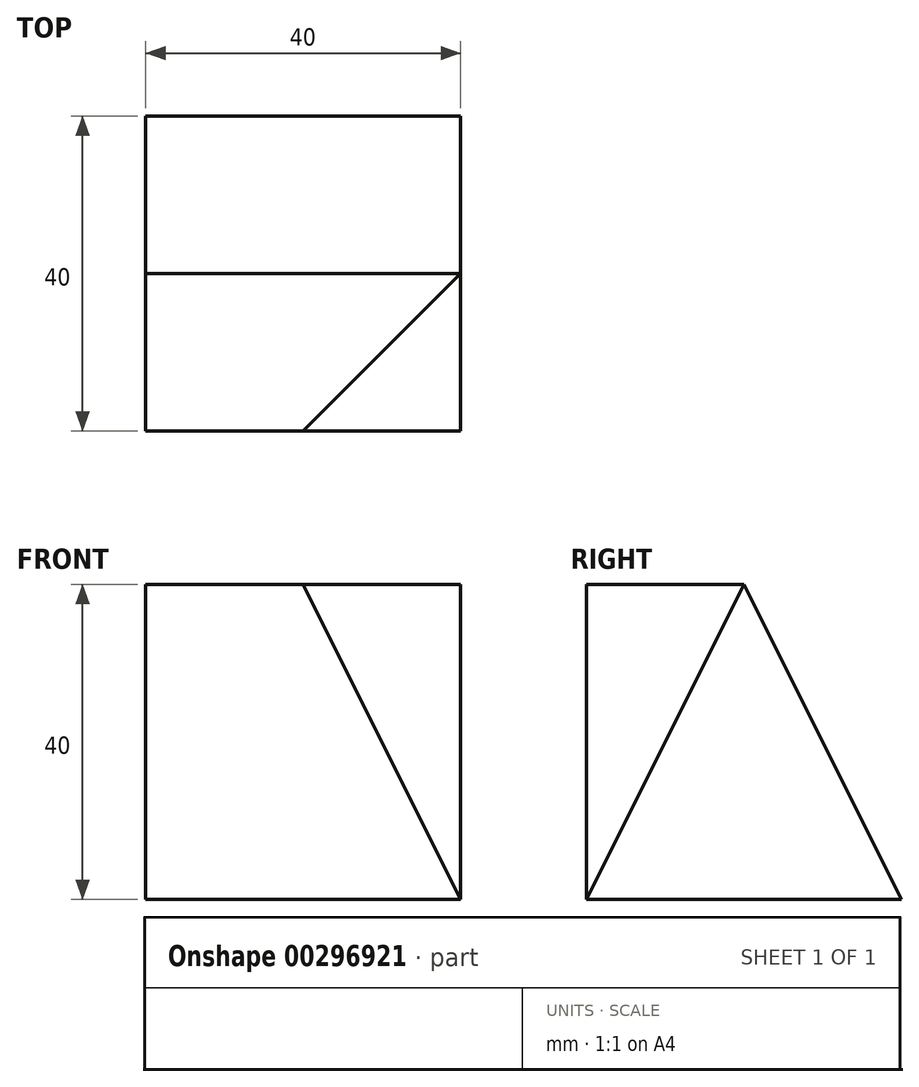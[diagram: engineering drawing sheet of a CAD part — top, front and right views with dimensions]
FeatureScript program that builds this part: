
annotation { "Feature Type Name" : "Feature", "Feature Type Description" : "" }
export const myFeature = defineFeature(function(context is Context, id is Id, definition is map)
    precondition{}
    {
        {
            var Q0;
            Q0=qCreatedBy(makeId("Right.planeOp"),FACE);
            var sketch = newSketch(context, id + "F0", { "sketchPlane" : qUnion([Q0])});
            skLineSegment(sketch, "E0.bottom", {"start": v(0, 0) * mm, "end": v(40, 0) * mm});
            skLineSegment(sketch, "E0.top", {"start": v(0, 40) * mm, "end": v(40, 40) * mm});
            skLineSegment(sketch, "E0.left", {"start": v(0, 0) * mm, "end": v(0, 40) * mm});
            skLineSegment(sketch, "E0.right", {"start": v(40, 0) * mm, "end": v(40, 40) * mm});
            skLineSegment(sketch, "E1", {"start": v(20, 40) * mm, "end": v(40, 0) * mm});
            skSolve(sketch);
        }
        {
            var Q0;
            Q0=makeQuery(id+"F0.imprint","IMPRINT",FACE,{"disambiguationData":[TD([[makeQuery(id+"F0.imprint","IMPRINT",EDGE,{"derivedFrom":sQuery(id+"F0.wireOp",EDGE,"E0.bottom")}),1.0]])]});
            extrude(context, id + "F1", {"entities" : qUnion([Q0]), "depth" : 40 * mm, "symmetric" : true});
        }
        {
            var Q0;
            Q0=makeQuery(id+"F1.opExtrude","SWEPT_EDGE",EDGE,{"disambiguationData":[OSD([sQuery(id+"F0.wireOp",EDGE,"E0.top"),sQuery(id+"F0.wireOp",EDGE,"E0.left")])]});
            cPoint(context, id + "F2", {"entities" : qUnion([Q0]), "parameter" : 0.5});
        }
        {
            var Q0;
            Q0=makeQuery(id+"F1.opExtrude","CAP_VERTEX",VERTEX,{"disambiguationData":[OSD([sQuery(id+"F0.wireOp",EDGE,"E0.top"),sQuery(id+"F0.wireOp",EDGE,"E1")])],"isStart":false});
            var Q1;
            Q1 = qCreatedBy(id + "F2" ,VERTEX);
            var Q2;
            Q2=makeQuery(id+"F1.opExtrude","CAP_VERTEX",VERTEX,{"disambiguationData":[OSD([sQuery(id+"F0.wireOp",EDGE,"E0.bottom"),sQuery(id+"F0.wireOp",EDGE,"E0.left")])],"isStart":false});
            cPlane(context, id + "F3", {"entities" : qUnion([Q0, Q1, Q2]), "cplaneType" : CPlaneType.THREE_POINT, "offset" : 25 * mm, "width" : 150 * mm, "height" : 150 * mm});
        }
        {
            var Q0;
            Q0=qCreatedBy(id+"F3.planeOp",FACE);
            var sketch = newSketch(context, id + "F4", { "sketchPlane" : qUnion([Q0])});
            skPoint(sketch, "E2.0", {"position": v(11.93, 35.78) * mm});
            skPoint(sketch, "E3.0", {"position": v(-14.9, 44.72) * mm});
            skPoint(sketch, "E4.0", {"position": v(-14.9, 0) * mm});
            skLineSegment(sketch, "E5", {"start": v(11.93, 35.78) * mm, "end": v(-14.9, 44.72) * mm});
            skLineSegment(sketch, "E6", {"start": v(-14.9, 0) * mm, "end": v(-14.9, 44.72) * mm});
            skLineSegment(sketch, "E7", {"start": v(-14.9, 0) * mm, "end": v(11.93, 35.78) * mm});
            skSolve(sketch);
        }
        {
            var Q0;
            Q0 = qSketchRegion(id + "F4", true);
            extrude(context, id + "F5", {"entities" : qUnion([Q0]), "operationType" : NewBodyOperationType.REMOVE, "endBound" : BoundingType.THROUGH_ALL, "oppositeDirection" : true, "depth" : 25 * mm});
        }
    });
